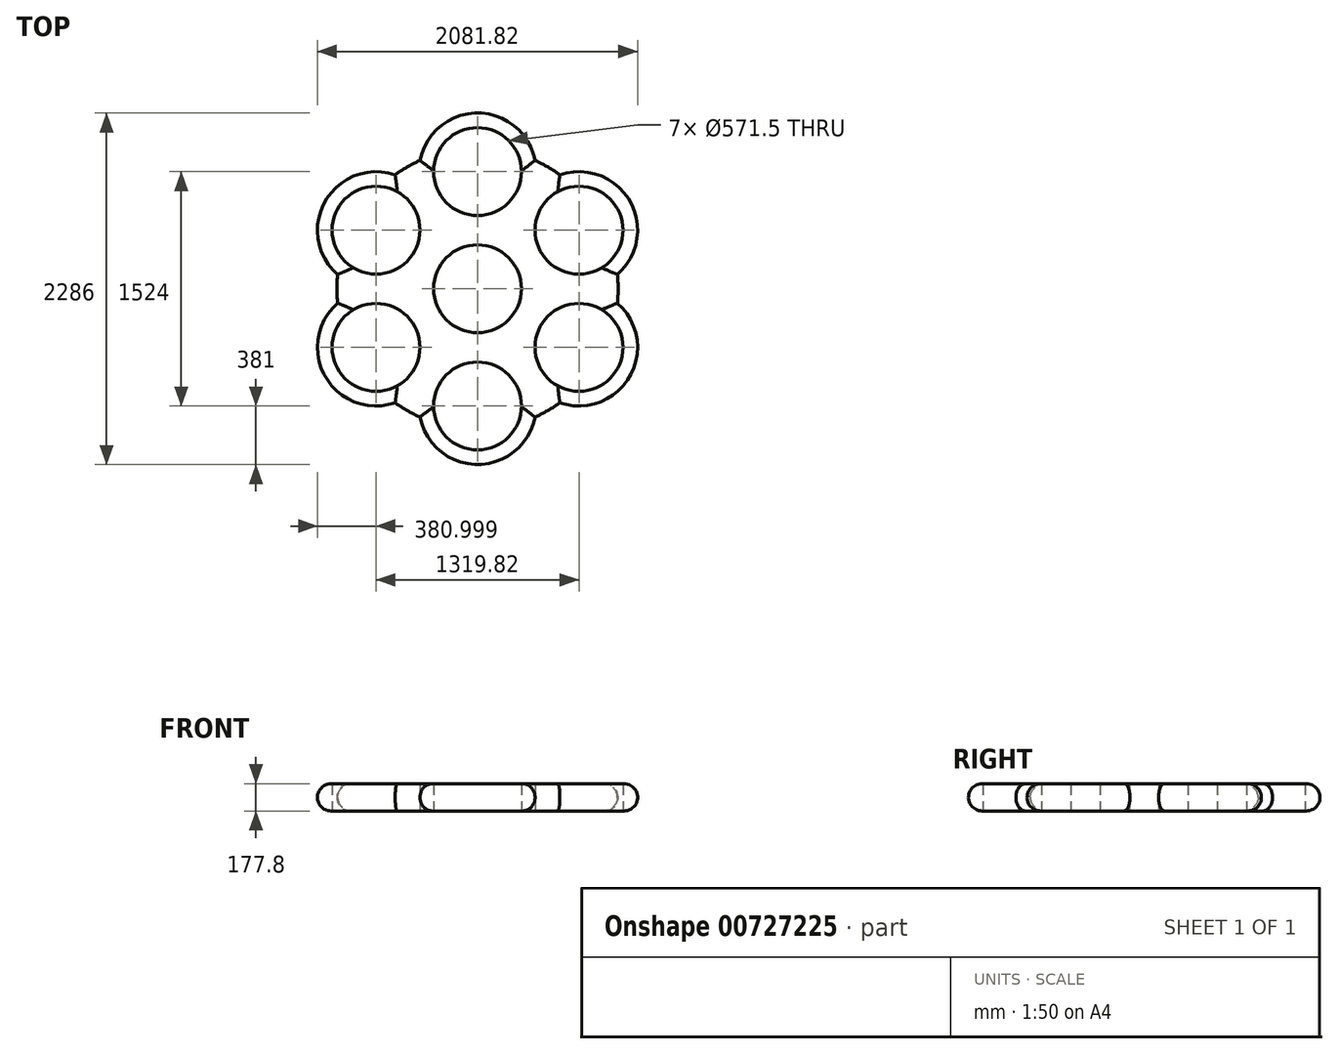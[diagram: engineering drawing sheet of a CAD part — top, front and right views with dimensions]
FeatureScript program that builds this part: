
annotation { "Feature Type Name" : "Feature", "Feature Type Description" : "" }
export const myFeature = defineFeature(function(context is Context, id is Id, definition is map)
    precondition{}
    {
        {
            var Q0;
            Q0=qCreatedBy(makeId("Top.planeOp"),FACE);
            var sketch = newSketch(context, id + "F0", { "sketchPlane" : qUnion([Q0])});
            skCircle(sketch, "E0", {"center": v(0, 0) * mm, "radius": 285.75 * mm});
            skCircle(sketch, "E1", {"center": v(0, 0) * mm, "radius": 381 * mm});
            skCircle(sketch, "E2", {"center": v(0, 0) * mm, "radius": 914.4 * mm});
            skLineSegment(sketch, "E3", {"start": v(0, 0) * mm, "end": v(0, 762) * mm});
            skCircle(sketch, "E4", {"center": v(0, 762) * mm, "radius": 285.75 * mm});
            skCircle(sketch, "E5", {"center": v(0, 762) * mm, "radius": 381 * mm});
            skCircle(sketch, "E6", {"center": v(-659.91, 381) * mm, "radius": 285.75 * mm});
            skCircle(sketch, "E7", {"center": v(-659.91, 381) * mm, "radius": 381 * mm});
            skCircle(sketch, "E8", {"center": v(-659.91, -381) * mm, "radius": 285.75 * mm});
            skCircle(sketch, "E9", {"center": v(-659.91, -381) * mm, "radius": 381 * mm});
            skCircle(sketch, "E10", {"center": v(0, -762) * mm, "radius": 285.75 * mm});
            skCircle(sketch, "E11", {"center": v(0, -762) * mm, "radius": 381 * mm});
            skCircle(sketch, "E12", {"center": v(659.91, -381) * mm, "radius": 285.75 * mm});
            skCircle(sketch, "E13", {"center": v(659.91, -381) * mm, "radius": 381 * mm});
            skCircle(sketch, "E14", {"center": v(659.91, 381) * mm, "radius": 285.75 * mm});
            skCircle(sketch, "E15", {"center": v(659.91, 381) * mm, "radius": 381 * mm});
            skSolve(sketch);
        }
        {
            var Q0;
            Q0 = qSketchRegion(id + "F0", true);
            var Q1;
            Q1=makeQuery(id+"F0.imprint","IMPRINT",FACE,{"disambiguationData":[TD([[makeQuery(id+"F0.imprint","IMPRINT",EDGE,{"derivedFrom":sQuery(id+"F0.wireOp",EDGE,"E0")}),-1.0]])]});
            var Q2;
            {var subQ0=sQuery(id+"F0.wireOp",EDGE,"E7");var subQ1=sQuery(id+"F0.wireOp",EDGE,"E1");var subQ2=makeQuery(id+"F0.imprint","INTERSECT",VERTEX,{"derivedFrom":[subQ1,subQ0]});Q2=makeQuery(id+"F0.imprint","IMPRINT",FACE,{"disambiguationData":[TD([[makeQuery(id+"F0.imprint","IMPRINT",EDGE,{"disambiguationData":[TD([[subQ2,-1.0]])],"derivedFrom":subQ0}),-1.0]])]});}
            var Q3;
            {var subQ0=sQuery(id+"F0.wireOp",EDGE,"E15");var subQ1=sQuery(id+"F0.wireOp",EDGE,"E1");var subQ2=makeQuery(id+"F0.imprint","INTERSECT",VERTEX,{"derivedFrom":[subQ1,subQ0]});Q3=makeQuery(id+"F0.imprint","IMPRINT",FACE,{"disambiguationData":[TD([[makeQuery(id+"F0.imprint","IMPRINT",EDGE,{"disambiguationData":[TD([[subQ2,1.0]])],"derivedFrom":subQ0}),-1.0]])]});}
            var Q4;
            {var subQ0=sQuery(id+"F0.wireOp",EDGE,"E15");var subQ1=sQuery(id+"F0.wireOp",EDGE,"E1");var subQ2=makeQuery(id+"F0.imprint","INTERSECT",VERTEX,{"derivedFrom":[subQ1,subQ0]});Q4=makeQuery(id+"F0.imprint","IMPRINT",FACE,{"disambiguationData":[TD([[makeQuery(id+"F0.imprint","IMPRINT",EDGE,{"disambiguationData":[TD([[subQ2,1.0]])],"derivedFrom":subQ1}),-1.0]])]});}
            var Q5;
            {var subQ0=sQuery(id+"F0.wireOp",EDGE,"E11");var subQ1=sQuery(id+"F0.wireOp",EDGE,"E1");var subQ2=makeQuery(id+"F0.imprint","INTERSECT",VERTEX,{"derivedFrom":[subQ1,subQ0]});Q5=makeQuery(id+"F0.imprint","IMPRINT",FACE,{"disambiguationData":[TD([[makeQuery(id+"F0.imprint","IMPRINT",EDGE,{"disambiguationData":[TD([[subQ2,-1.0]])],"derivedFrom":subQ1}),-1.0]])]});}
            var Q6;
            {var subQ0=sQuery(id+"F0.wireOp",EDGE,"E9");var subQ1=sQuery(id+"F0.wireOp",EDGE,"E1");var subQ2=makeQuery(id+"F0.imprint","INTERSECT",VERTEX,{"derivedFrom":[subQ1,subQ0]});Q6=makeQuery(id+"F0.imprint","IMPRINT",FACE,{"disambiguationData":[TD([[makeQuery(id+"F0.imprint","IMPRINT",EDGE,{"disambiguationData":[TD([[subQ2,-1.0]])],"derivedFrom":subQ1}),-1.0]])]});}
            var Q7;
            {var subQ0=sQuery(id+"F0.wireOp",EDGE,"E7");var subQ1=sQuery(id+"F0.wireOp",EDGE,"E1");var subQ2=makeQuery(id+"F0.imprint","INTERSECT",VERTEX,{"derivedFrom":[subQ1,subQ0]});Q7=makeQuery(id+"F0.imprint","IMPRINT",FACE,{"disambiguationData":[TD([[makeQuery(id+"F0.imprint","IMPRINT",EDGE,{"disambiguationData":[TD([[subQ2,-1.0]])],"derivedFrom":subQ1}),-1.0]])]});}
            extrude(context, id + "F1", {"entities" : qUnion([Q0, Q1, Q2, Q3, Q4, Q5, Q6, Q7]), "depth" : 177.8 * mm, "offsetDistance" : 25.4 * mm});
        }
        {
            var Q0;
            Q0=makeQuery(id+"F1.opExtrude","CAP_EDGE",EDGE,{"disambiguationData":[OSD([sQuery(id+"F0.wireOp",EDGE,"E7")])],"isStart":false});
            var Q1;
            Q1=makeQuery(id+"F1.opExtrude","CAP_EDGE",EDGE,{"disambiguationData":[OSD([sQuery(id+"F0.wireOp",EDGE,"E9")])],"isStart":false});
            var Q2;
            Q2=makeQuery(id+"F1.opExtrude","CAP_EDGE",EDGE,{"disambiguationData":[OSD([sQuery(id+"F0.wireOp",EDGE,"E11")])],"isStart":false});
            var Q3;
            Q3=makeQuery(id+"F1.opExtrude","CAP_EDGE",EDGE,{"disambiguationData":[OSD([sQuery(id+"F0.wireOp",EDGE,"E13")])],"isStart":true});
            var Q4;
            Q4=makeQuery(id+"F1.opExtrude","CAP_EDGE",EDGE,{"disambiguationData":[OSD([sQuery(id+"F0.wireOp",EDGE,"E15")])],"isStart":false});
            var Q5;
            {var subQ0=sQuery(id+"F0.wireOp",EDGE,"E2");Q5=makeQuery(id+"F1.opExtrude","CAP_EDGE",EDGE,{"disambiguationData":[OSD([subQ0]),TDD([makeQuery(id+"F0.imprint","IMPRINT",EDGE,{"disambiguationData":[TD([[makeQuery(id+"F0.imprint","INTERSECT",VERTEX,{"disambiguationData":[OD(1.0)],"derivedFrom":[subQ0,sQuery(id+"F0.wireOp",EDGE,"E15")]}),-1.0]])],"derivedFrom":subQ0})])],"isStart":false});}
            var Q6;
            {var subQ0=sQuery(id+"F0.wireOp",EDGE,"E2");Q6=makeQuery(id+"F1.opExtrude","CAP_EDGE",EDGE,{"disambiguationData":[OSD([subQ0]),TDD([makeQuery(id+"F0.imprint","IMPRINT",EDGE,{"disambiguationData":[TD([[makeQuery(id+"F0.imprint","INTERSECT",VERTEX,{"disambiguationData":[OD(1.0)],"derivedFrom":[subQ0,sQuery(id+"F0.wireOp",EDGE,"E5")]}),-1.0]])],"derivedFrom":subQ0})])],"isStart":false});}
            var Q7;
            {var subQ0=sQuery(id+"F0.wireOp",EDGE,"E2");Q7=makeQuery(id+"F1.opExtrude","CAP_EDGE",EDGE,{"disambiguationData":[OSD([subQ0]),TDD([makeQuery(id+"F0.imprint","IMPRINT",EDGE,{"disambiguationData":[TD([[makeQuery(id+"F0.imprint","INTERSECT",VERTEX,{"disambiguationData":[OD(1.0)],"derivedFrom":[subQ0,sQuery(id+"F0.wireOp",EDGE,"E7")]}),-1.0]])],"derivedFrom":subQ0})])],"isStart":false});}
            var Q8;
            {var subQ0=sQuery(id+"F0.wireOp",EDGE,"E2");Q8=makeQuery(id+"F1.opExtrude","CAP_EDGE",EDGE,{"disambiguationData":[OSD([subQ0]),TDD([makeQuery(id+"F0.imprint","IMPRINT",EDGE,{"disambiguationData":[TD([[makeQuery(id+"F0.imprint","INTERSECT",VERTEX,{"disambiguationData":[OD(1.0)],"derivedFrom":[subQ0,sQuery(id+"F0.wireOp",EDGE,"E9")]}),-1.0]])],"derivedFrom":subQ0})])],"isStart":false});}
            var Q9;
            {var subQ0=sQuery(id+"F0.wireOp",EDGE,"E2");Q9=makeQuery(id+"F1.opExtrude","CAP_EDGE",EDGE,{"disambiguationData":[OSD([subQ0]),TDD([makeQuery(id+"F0.imprint","IMPRINT",EDGE,{"disambiguationData":[TD([[makeQuery(id+"F0.imprint","INTERSECT",VERTEX,{"disambiguationData":[OD(1.0)],"derivedFrom":[subQ0,sQuery(id+"F0.wireOp",EDGE,"E11")]}),-1.0]])],"derivedFrom":subQ0})])],"isStart":true});}
            var Q10;
            {var subQ0=sQuery(id+"F0.wireOp",EDGE,"E2");Q10=makeQuery(id+"F1.opExtrude","CAP_EDGE",EDGE,{"disambiguationData":[OSD([subQ0]),TDD([makeQuery(id+"F0.imprint","IMPRINT",EDGE,{"disambiguationData":[TD([[makeQuery(id+"F0.imprint","INTERSECT",VERTEX,{"disambiguationData":[OD(0.0)],"derivedFrom":[subQ0,sQuery(id+"F0.wireOp",EDGE,"E15")]}),1.0]])],"derivedFrom":subQ0})])],"isStart":false});}
            var Q11;
            {var subQ0=sQuery(id+"F0.wireOp",EDGE,"E2");Q11=makeQuery(id+"F1.opExtrude","CAP_EDGE",EDGE,{"disambiguationData":[OSD([subQ0]),TDD([makeQuery(id+"F0.imprint","IMPRINT",EDGE,{"disambiguationData":[TD([[makeQuery(id+"F0.imprint","INTERSECT",VERTEX,{"disambiguationData":[OD(1.0)],"derivedFrom":[subQ0,sQuery(id+"F0.wireOp",EDGE,"E11")]}),-1.0]])],"derivedFrom":subQ0})])],"isStart":false});}
            var Q12;
            Q12=makeQuery(id+"F1.opExtrude","CAP_EDGE",EDGE,{"disambiguationData":[OSD([sQuery(id+"F0.wireOp",EDGE,"E13")])],"isStart":false});
            var Q13;
            {var subQ0=sQuery(id+"F0.wireOp",EDGE,"E2");Q13=makeQuery(id+"F1.opExtrude","CAP_EDGE",EDGE,{"disambiguationData":[OSD([subQ0]),TDD([makeQuery(id+"F0.imprint","IMPRINT",EDGE,{"disambiguationData":[TD([[makeQuery(id+"F0.imprint","INTERSECT",VERTEX,{"disambiguationData":[OD(0.0)],"derivedFrom":[subQ0,sQuery(id+"F0.wireOp",EDGE,"E15")]}),1.0]])],"derivedFrom":subQ0})])],"isStart":true});}
            var Q14;
            Q14=makeQuery(id+"F1.opExtrude","CAP_EDGE",EDGE,{"disambiguationData":[OSD([sQuery(id+"F0.wireOp",EDGE,"E15")])],"isStart":true});
            var Q15;
            {var subQ0=sQuery(id+"F0.wireOp",EDGE,"E2");Q15=makeQuery(id+"F1.opExtrude","CAP_EDGE",EDGE,{"disambiguationData":[OSD([subQ0]),TDD([makeQuery(id+"F0.imprint","IMPRINT",EDGE,{"disambiguationData":[TD([[makeQuery(id+"F0.imprint","INTERSECT",VERTEX,{"disambiguationData":[OD(1.0)],"derivedFrom":[subQ0,sQuery(id+"F0.wireOp",EDGE,"E15")]}),-1.0]])],"derivedFrom":subQ0})])],"isStart":true});}
            var Q16;
            Q16=makeQuery(id+"F1.opExtrude","CAP_EDGE",EDGE,{"disambiguationData":[OSD([sQuery(id+"F0.wireOp",EDGE,"E5")])],"isStart":false});
            var Q17;
            Q17=makeQuery(id+"F1.opExtrude","CAP_EDGE",EDGE,{"disambiguationData":[OSD([sQuery(id+"F0.wireOp",EDGE,"E11")])],"isStart":true});
            var Q18;
            Q18=makeQuery(id+"F1.opExtrude","CAP_EDGE",EDGE,{"disambiguationData":[OSD([sQuery(id+"F0.wireOp",EDGE,"E9")])],"isStart":true});
            var Q19;
            {var subQ0=sQuery(id+"F0.wireOp",EDGE,"E2");Q19=makeQuery(id+"F1.opExtrude","CAP_EDGE",EDGE,{"disambiguationData":[OSD([subQ0]),TDD([makeQuery(id+"F0.imprint","IMPRINT",EDGE,{"disambiguationData":[TD([[makeQuery(id+"F0.imprint","INTERSECT",VERTEX,{"disambiguationData":[OD(1.0)],"derivedFrom":[subQ0,sQuery(id+"F0.wireOp",EDGE,"E9")]}),-1.0]])],"derivedFrom":subQ0})])],"isStart":true});}
            var Q20;
            {var subQ0=sQuery(id+"F0.wireOp",EDGE,"E2");Q20=makeQuery(id+"F1.opExtrude","CAP_EDGE",EDGE,{"disambiguationData":[OSD([subQ0]),TDD([makeQuery(id+"F0.imprint","IMPRINT",EDGE,{"disambiguationData":[TD([[makeQuery(id+"F0.imprint","INTERSECT",VERTEX,{"disambiguationData":[OD(1.0)],"derivedFrom":[subQ0,sQuery(id+"F0.wireOp",EDGE,"E7")]}),-1.0]])],"derivedFrom":subQ0})])],"isStart":true});}
            var Q21;
            Q21=makeQuery(id+"F1.opExtrude","CAP_EDGE",EDGE,{"disambiguationData":[OSD([sQuery(id+"F0.wireOp",EDGE,"E7")])],"isStart":true});
            var Q22;
            {var subQ0=sQuery(id+"F0.wireOp",EDGE,"E2");Q22=makeQuery(id+"F1.opExtrude","CAP_EDGE",EDGE,{"disambiguationData":[OSD([subQ0]),TDD([makeQuery(id+"F0.imprint","IMPRINT",EDGE,{"disambiguationData":[TD([[makeQuery(id+"F0.imprint","INTERSECT",VERTEX,{"disambiguationData":[OD(1.0)],"derivedFrom":[subQ0,sQuery(id+"F0.wireOp",EDGE,"E5")]}),-1.0]])],"derivedFrom":subQ0})])],"isStart":true});}
            var Q23;
            Q23=makeQuery(id+"F1.opExtrude","CAP_EDGE",EDGE,{"disambiguationData":[OSD([sQuery(id+"F0.wireOp",EDGE,"E5")])],"isStart":true});
            fillet(context, id + "F2", {"entities" : qUnion([Q0, Q1, Q2, Q3, Q4, Q5, Q6, Q7, Q8, Q9, Q10, Q11, Q12, Q13, Q14, Q15, Q16, Q17, Q18, Q19, Q20, Q21, Q22, Q23]), "radius" : 88.9 * mm, "tangentPropagation" : true, "allowEdgeOverflow" : false});
        }
    });
